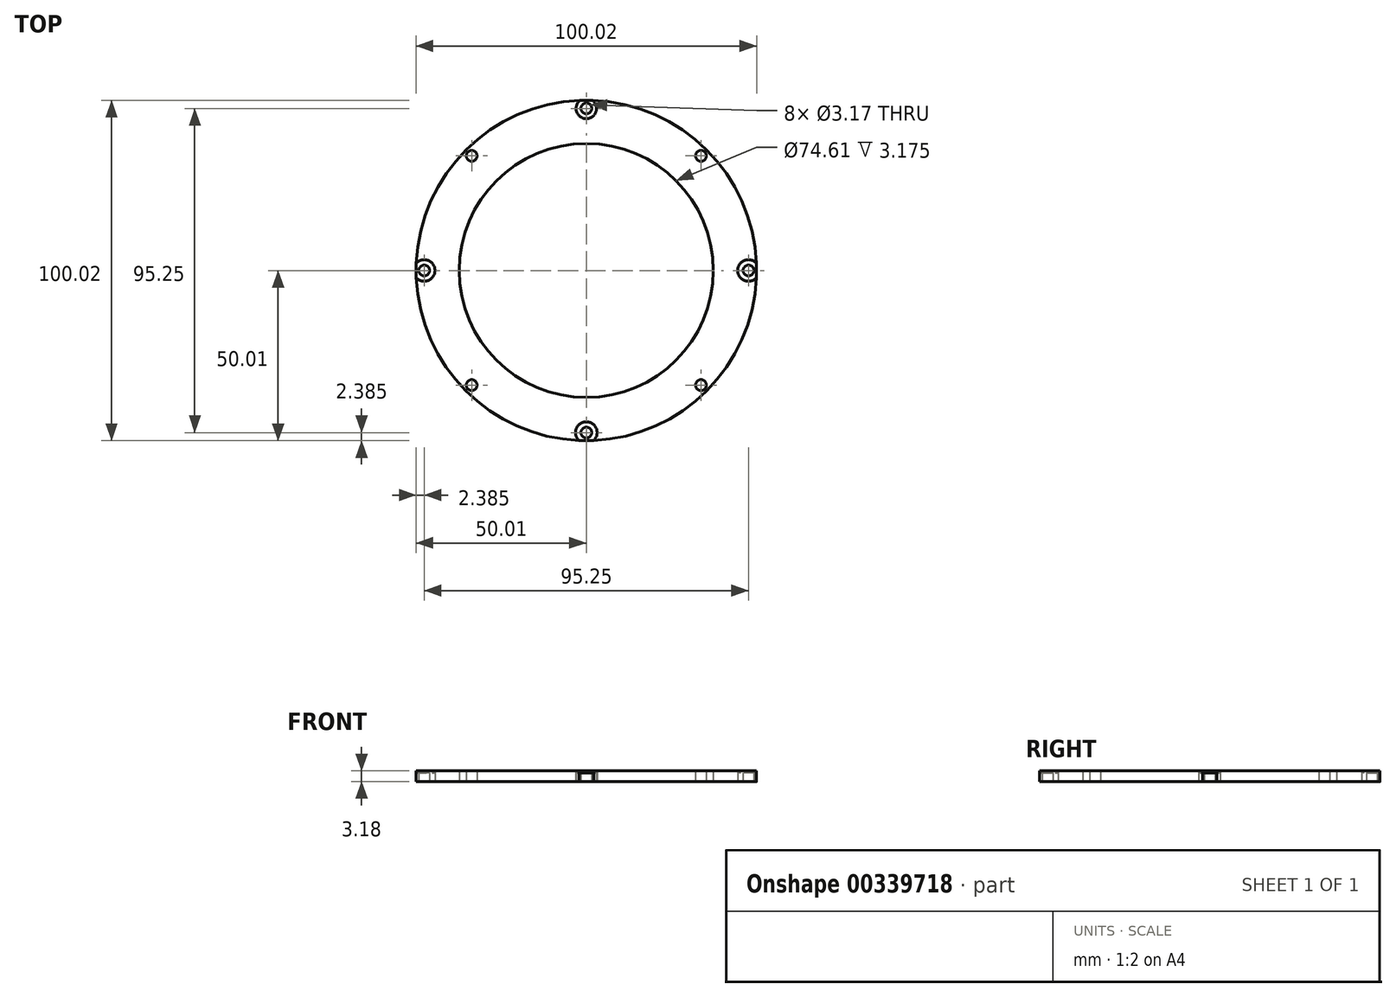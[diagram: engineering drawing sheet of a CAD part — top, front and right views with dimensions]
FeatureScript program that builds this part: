
annotation { "Feature Type Name" : "Feature", "Feature Type Description" : "" }
export const myFeature = defineFeature(function(context is Context, id is Id, definition is map)
    precondition{}
    {
        {
            var Q0;
            Q0=qCreatedBy(makeId("Top.planeOp"),FACE);
            var sketch = newSketch(context, id + "F0", { "sketchPlane" : qUnion([Q0])});
            skCircle(sketch, "E0", {"center": v(0, 0) * mm, "radius": 50 * mm});
            skCircle(sketch, "E1", {"center": v(0, 0) * mm, "radius": 37.3 * mm});
            skCircle(sketch, "E2", {"center": v(0, 0) * mm, "radius": 29.37 * mm});
            skCircle(sketch, "E3", {"center": v(0, 47.63) * mm, "radius": 1.59 * mm});
            skCircle(sketch, "E4.1.0", {"center": v(-33.68, 33.68) * mm, "radius": 1.59 * mm});
            skCircle(sketch, "E4.2.0", {"center": v(-47.63, 0) * mm, "radius": 1.59 * mm});
            skCircle(sketch, "E4.3.0", {"center": v(-33.68, -33.68) * mm, "radius": 1.59 * mm});
            skCircle(sketch, "E4.4.0", {"center": v(0, -47.63) * mm, "radius": 1.59 * mm});
            skCircle(sketch, "E4.5.0", {"center": v(33.68, -33.68) * mm, "radius": 1.59 * mm});
            skCircle(sketch, "E4.6.0", {"center": v(47.63, 0) * mm, "radius": 1.59 * mm});
            skCircle(sketch, "E4.7.0", {"center": v(33.68, 33.68) * mm, "radius": 1.59 * mm});
            skArc(sketch, "E5", {"start": v(-49.96, -2.15) * mm, "mid": v(-44.45, 0) * mm, "end": v(-49.96, 2.15) * mm});
            skArc(sketch, "E6", {"start": v(49.96, 2.15) * mm, "mid": v(44.45, 0) * mm, "end": v(49.96, -2.15) * mm});
            skArc(sketch, "E7", {"start": v(2.15, -49.96) * mm, "mid": v(0, -44.45) * mm, "end": v(-2.15, -49.96) * mm});
            skArc(sketch, "E8", {"start": v(-1.88, 49.97) * mm, "mid": v(0, 44.62) * mm, "end": v(1.88, 49.97) * mm});
            skSolve(sketch);
        }
        {
            var Q0;
            Q0=makeQuery(id+"F0.imprint","IMPRINT",FACE,{"disambiguationData":[TD([[makeQuery(id+"F0.imprint","IMPRINT",EDGE,{"derivedFrom":sQuery(id+"F0.wireOp",EDGE,"E3")}),-1.0]])]});
            var Q1;
            Q1=makeQuery(id+"F0.imprint","IMPRINT",FACE,{"disambiguationData":[TD([[makeQuery(id+"F0.imprint","IMPRINT",EDGE,{"derivedFrom":sQuery(id+"F0.wireOp",EDGE,"E4.2.0")}),-1.0]])]});
            var Q2;
            Q2=makeQuery(id+"F0.imprint","IMPRINT",FACE,{"disambiguationData":[TD([[makeQuery(id+"F0.imprint","IMPRINT",EDGE,{"derivedFrom":sQuery(id+"F0.wireOp",EDGE,"E4.4.0")}),-1.0]])]});
            var Q3;
            Q3=makeQuery(id+"F0.imprint","IMPRINT",FACE,{"disambiguationData":[TD([[makeQuery(id+"F0.imprint","IMPRINT",EDGE,{"derivedFrom":sQuery(id+"F0.wireOp",EDGE,"E4.6.0")}),-1.0]])]});
            extrude(context, id + "F1", {"entities" : qUnion([Q0, Q1, Q2, Q3]), "depth" : 2.54 * mm});
        }
        {
            var Q0;
            Q0=makeQuery(id+"F0.imprint","IMPRINT",FACE,{"disambiguationData":[TD([[makeQuery(id+"F0.imprint","IMPRINT",EDGE,{"derivedFrom":sQuery(id+"F0.wireOp",EDGE,"E1")}),-1.0]])]});
            extrude(context, id + "F2", {"entities" : qUnion([Q0]), "depth" : 3.17 * mm});
        }
    });
